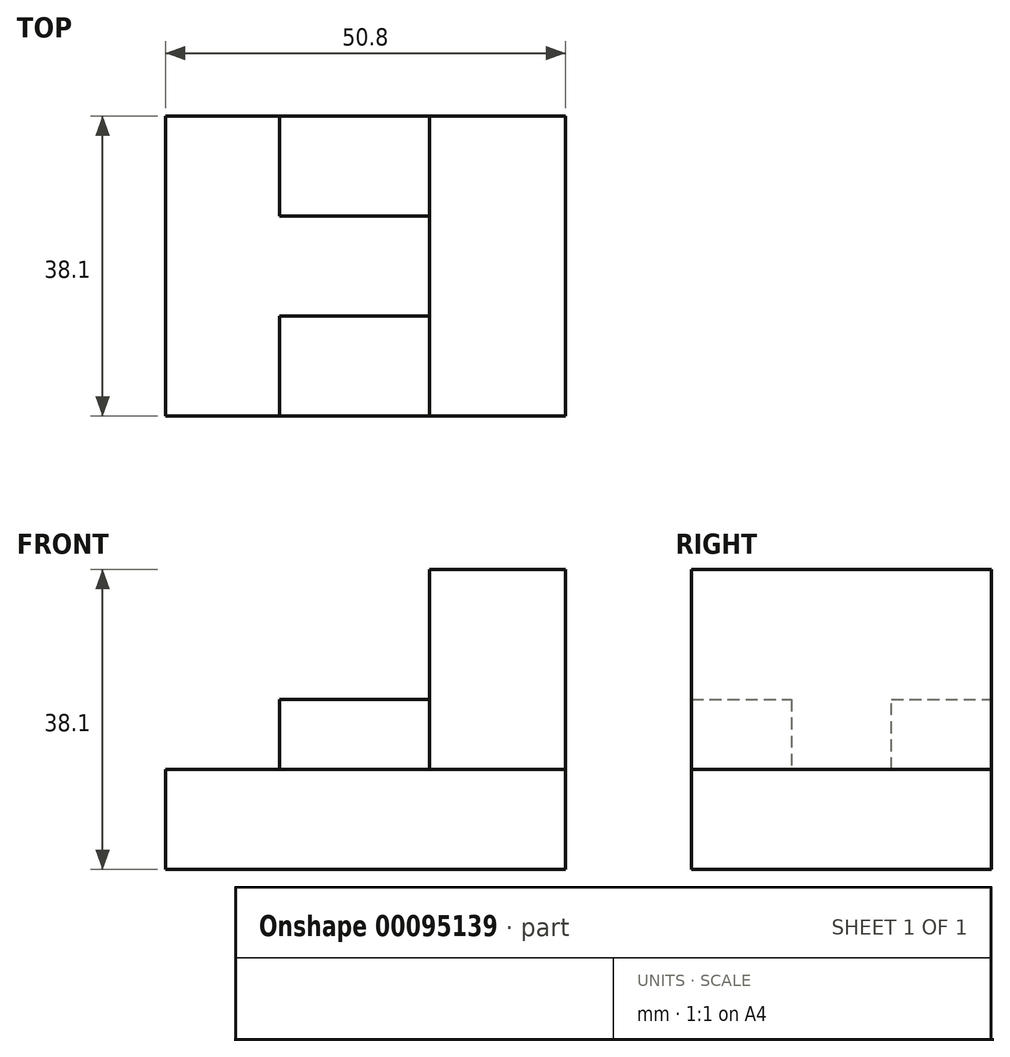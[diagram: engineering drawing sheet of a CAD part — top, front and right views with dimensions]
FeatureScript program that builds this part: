
annotation { "Feature Type Name" : "Feature", "Feature Type Description" : "" }
export const myFeature = defineFeature(function(context is Context, id is Id, definition is map)
    precondition{}
    {
        {
            var Q0;
            Q0=qCreatedBy(makeId("Front.planeOp"),FACE);
            var sketch = newSketch(context, id + "F0", { "sketchPlane" : qUnion([Q0])});
            skLineSegment(sketch, "E0.bottom", {"start": v(-25.4, 6.35) * mm, "end": v(25.4, 6.35) * mm});
            skLineSegment(sketch, "E0.top", {"start": v(-25.4, -6.35) * mm, "end": v(25.4, -6.35) * mm});
            skLineSegment(sketch, "E0.left", {"start": v(-25.4, 6.35) * mm, "end": v(-25.4, -6.35) * mm});
            skLineSegment(sketch, "E0.right", {"start": v(25.4, 6.35) * mm, "end": v(25.4, -6.35) * mm});
            skPoint(sketch, "E0.middle", {"position": v(0, 0) * mm});
            skSolve(sketch);
        }
        {
            var Q0;
            Q0=makeQuery(id+"F0.imprint","IMPRINT",FACE,{"disambiguationData":[TD([[makeQuery(id+"F0.imprint","IMPRINT",EDGE,{"derivedFrom":sQuery(id+"F0.wireOp",EDGE,"E0.bottom")}),-1.0]])]});
            extrude(context, id + "F1", {"entities" : qUnion([Q0]), "depth" : 38.1 * mm});
        }
        {
            var Q0;
            Q0=qCreatedBy(makeId("Front.planeOp"),FACE);
            var sketch = newSketch(context, id + "F2", { "sketchPlane" : qUnion([Q0])});
            skLineSegment(sketch, "E1.bottom", {"start": v(-10.92, 6.35) * mm, "end": v(8.13, 6.35) * mm});
            skLineSegment(sketch, "E1.top", {"start": v(-10.92, 15.24) * mm, "end": v(8.13, 15.24) * mm});
            skLineSegment(sketch, "E1.left", {"start": v(-10.92, 6.35) * mm, "end": v(-10.92, 15.24) * mm});
            skLineSegment(sketch, "E1.right", {"start": v(8.13, 6.35) * mm, "end": v(8.13, 15.24) * mm});
            skSolve(sketch);
        }
        {
            var Q0;
            Q0=makeQuery(id+"F2.imprint","IMPRINT",FACE,{"disambiguationData":[TD([[makeQuery(id+"F2.imprint","IMPRINT",EDGE,{"derivedFrom":sQuery(id+"F2.wireOp",EDGE,"E1.bottom")}),1.0]])]});
            extrude(context, id + "F3", {"entities" : qUnion([Q0]), "depth" : 12.7 * mm});
        }
        {
            var Q0;
            Q0=qCreatedBy(makeId("Front.planeOp"),FACE);
            var sketch = newSketch(context, id + "F4", { "sketchPlane" : qUnion([Q0])});
            skLineSegment(sketch, "E2.bottom", {"start": v(25.4, 6.35) * mm, "end": v(8.13, 6.35) * mm});
            skLineSegment(sketch, "E2.top", {"start": v(25.4, 31.75) * mm, "end": v(8.13, 31.75) * mm});
            skLineSegment(sketch, "E2.left", {"start": v(25.4, 6.35) * mm, "end": v(25.4, 31.75) * mm});
            skLineSegment(sketch, "E2.right", {"start": v(8.13, 6.35) * mm, "end": v(8.13, 31.75) * mm});
            skSolve(sketch);
        }
        {
            var Q0;
            Q0=makeQuery(id+"F4.imprint","IMPRINT",FACE,{"disambiguationData":[TD([[makeQuery(id+"F4.imprint","IMPRINT",EDGE,{"derivedFrom":sQuery(id+"F4.wireOp",EDGE,"E2.bottom")}),-1.0]])]});
            extrude(context, id + "F5", {"entities" : qUnion([Q0]), "depth" : 38.1 * mm});
        }
        {
            var Q0;
            Q0=makeQuery(id+"F1.opExtrude","SWEPT_FACE",FACE,{"disambiguationData":[OSD([sQuery(id+"F0.wireOp",EDGE,"E0.bottom")])]});
            var sketch = newSketch(context, id + "F6", { "sketchPlane" : qUnion([Q0])});
            skLineSegment(sketch, "E3.bottom", {"start": v(8.13, -38.1) * mm, "end": v(-10.92, -38.1) * mm});
            skLineSegment(sketch, "E3.top", {"start": v(8.13, -25.4) * mm, "end": v(-10.92, -25.4) * mm});
            skLineSegment(sketch, "E3.left", {"start": v(8.13, -38.1) * mm, "end": v(8.13, -25.4) * mm});
            skLineSegment(sketch, "E3.right", {"start": v(-10.92, -38.1) * mm, "end": v(-10.92, -25.4) * mm});
            skSolve(sketch);
        }
        {
            var Q0;
            Q0 = qSketchRegion(id + "F6", true);
            extrude(context, id + "F7", {"entities" : qUnion([Q0]), "depth" : 8.9 * mm});
        }
    });
